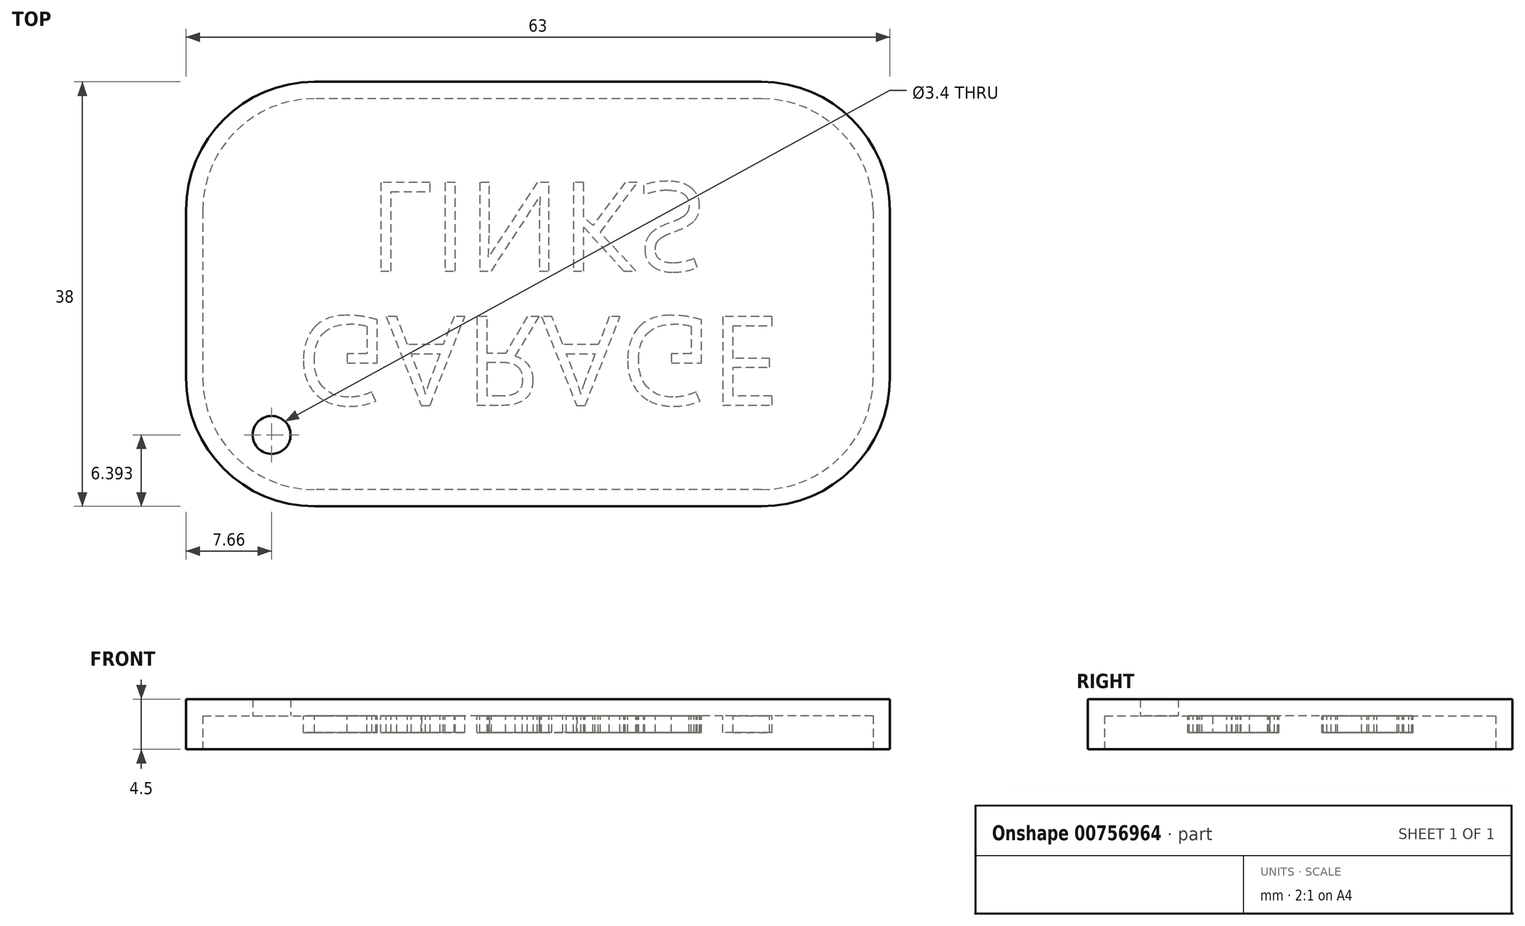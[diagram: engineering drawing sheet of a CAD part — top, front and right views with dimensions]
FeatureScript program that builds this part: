
annotation { "Feature Type Name" : "Feature", "Feature Type Description" : "" }
export const myFeature = defineFeature(function(context is Context, id is Id, definition is map)
    precondition{}
    {
        {
            var Q0;
            Q0=qCreatedBy(makeId("Top.planeOp"),FACE);
            var sketch = newSketch(context, id + "F0", { "sketchPlane" : qUnion([Q0])});
            skLineSegment(sketch, "E0.bottom", {"start": v(30, 17.5) * mm, "end": v(-30, 17.5) * mm});
            skLineSegment(sketch, "E0.top", {"start": v(30, -17.5) * mm, "end": v(-30, -17.5) * mm});
            skLineSegment(sketch, "E0.left", {"start": v(30, 17.5) * mm, "end": v(30, -17.5) * mm});
            skLineSegment(sketch, "E0.right", {"start": v(-30, 17.5) * mm, "end": v(-30, -17.5) * mm});
            skPoint(sketch, "E0.middle", {"position": v(0, 0) * mm});
            skSolve(sketch);
        }
        {
            var Q0;
            Q0=makeQuery(id+"F0.imprint","IMPRINT",FACE,{"disambiguationData":[TD([[makeQuery(id+"F0.imprint","IMPRINT",EDGE,{"derivedFrom":sQuery(id+"F0.wireOp",EDGE,"E0.bottom")}),1.0]])]});
            extrude(context, id + "F1", {"entities" : qUnion([Q0]), "depth" : 3 * mm, "offsetDistance" : 25 * mm});
        }
        {
            var Q0;
            Q0=makeQuery(id+"F1.opExtrude","SWEPT_EDGE",EDGE,{"disambiguationData":[OSD([sQuery(id+"F0.wireOp",EDGE,"E0.bottom"),sQuery(id+"F0.wireOp",EDGE,"E0.left")])]});
            var Q1;
            Q1=makeQuery(id+"F1.opExtrude","SWEPT_EDGE",EDGE,{"disambiguationData":[OSD([sQuery(id+"F0.wireOp",EDGE,"E0.top"),sQuery(id+"F0.wireOp",EDGE,"E0.right")])]});
            var Q2;
            Q2=makeQuery(id+"F1.opExtrude","SWEPT_EDGE",EDGE,{"disambiguationData":[OSD([sQuery(id+"F0.wireOp",EDGE,"E0.top"),sQuery(id+"F0.wireOp",EDGE,"E0.left")])]});
            var Q3;
            Q3=makeQuery(id+"F1.opExtrude","SWEPT_EDGE",EDGE,{"disambiguationData":[OSD([sQuery(id+"F0.wireOp",EDGE,"E0.bottom"),sQuery(id+"F0.wireOp",EDGE,"E0.right")])]});
            fillet(context, id + "F2", {"entities" : qUnion([Q0, Q1, Q2, Q3]), "radius" : 10 * mm, "tangentPropagation" : true, "allowEdgeOverflow" : false});
        }
        {
            var Q0;
            Q0=makeQuery(id+"F1.opExtrude","CAP_FACE",FACE,{"disambiguationData":[OSD([sQuery(id+"F0.wireOp",EDGE,"E0.bottom"),sQuery(id+"F0.wireOp",EDGE,"E0.top"),sQuery(id+"F0.wireOp",EDGE,"E0.left"),sQuery(id+"F0.wireOp",EDGE,"E0.right")])],"isStart":true});
            shell(context, id + "F3", {"entities" : qUnion([Q0]), "thickness" : 1.5 * mm, "oppositeDirection" : true});
        }
        {
            var Q0;
            Q0=makeQuery(id+"F3.opShell","OFFSET_FACE",FACE,{"disambiguationData":[OSD([sQuery(id+"F0.wireOp",EDGE,"E0.bottom"),sQuery(id+"F0.wireOp",EDGE,"E0.top"),sQuery(id+"F0.wireOp",EDGE,"E0.left"),sQuery(id+"F0.wireOp",EDGE,"E0.right")])]});
            var sketch = newSketch(context, id + "F4", { "sketchPlane" : qUnion([Q0])});
            skText(sketch, "E1", { "text": "GARAGE", "fontName": "OpenSans-Regular.ttf"});
            skText(sketch, "E2", { "text": "LINKS", "fontName": "OpenSans-Regular.ttf"});
            const initialGuessF4  = {"E1": [-0.02167, 0.002, 1, 0, 0.008], "E2": [-0.01517, -0.01, 1, 0, 0.008]};
            skSetInitialGuess(sketch, initialGuessF4);
            skSolve(sketch);
        }
        {
            var Q0;
            Q0=qSketchRegion(id+"F4",true);
            extrude(context, id + "F5", {"entities" : qUnion([Q0]), "operationType" : NewBodyOperationType.ADD, "depth" : 1.5 * mm, "offsetDistance" : 25 * mm});
        }
        {
            var Q0;
            {var subQ0=sQuery(id+"F0.wireOp",EDGE,"E0.right");var subQ1=sQuery(id+"F0.wireOp",EDGE,"E0.top");var subQ2=sQuery(id+"F0.wireOp",EDGE,"E0.left");var subQ3=sQuery(id+"F0.wireOp",EDGE,"E0.bottom");Q0=makeQuery(id+"F5.boolean.opBoolean","SPLIT",FACE,{"disambiguationData":[TD([makeQuery(id+"F3.opShell","OFFSET_FACE",FACE,{"disambiguationData":[OSD([subQ3])]})])],"derivedFrom":makeQuery(id+"F3.opShell","OFFSET_FACE",FACE,{"disambiguationData":[OSD([subQ3,subQ1,subQ2,subQ0])]})});}
            var sketch = newSketch(context, id + "F6", { "sketchPlane" : qUnion([Q0])});
            skPoint(sketch, "E3", {"position": v(-23.84, 12.6) * mm});
            skSolve(sketch);
        }
        {
            var Q0;
            Q0=sQuery(id+"F6.wireOp",VERTEX,"E3");
            var Q1;
            Q1=makeQuery(id+"F1.opExtrude","SWEPT_BODY",BODY,{"disambiguationData":[OSD([sQuery(id+"F0.wireOp",EDGE,"E0.bottom"),sQuery(id+"F0.wireOp",EDGE,"E0.top"),sQuery(id+"F0.wireOp",EDGE,"E0.left"),sQuery(id+"F0.wireOp",EDGE,"E0.right")])]});
            hole(context, id + "F7", {"style" : HoleStyle.SIMPLE, "endStyle" : HoleEndStyle.THROUGH, "holeDiameter" : 3.4 * mm, "majorDiameter" : 5 * mm, "isTappedThrough" : true, "tappedDepth" : 12 * mm, "tapClearance" : 3, "locations" : qUnion([Q0]), "scope" : qUnion([Q1])});
        }
    });
